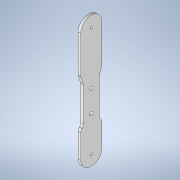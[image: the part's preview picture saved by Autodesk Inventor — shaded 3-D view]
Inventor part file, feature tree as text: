
AUTODESK INVENTOR PART (.ipt)
format: ipt  version: 2022 (Build 260153000, 153)  size: 157,184 bytes
history: native  units: mm
features: extrude x1, sketch x1
ambient origin geometry x8: Origin, YZ Plane, XZ Plane, XY Plane, X Axis, Y Axis, Z Axis, Center Point
bodies: Solid1 (feature_tree)
feature tree (2):
  extrude  "Extrusion1"  Depth=5.0mm
  sketch  "Sketch1"  dims[d16=3.0mm d17=0.0mm d44=4.0mm d46=8.0mm d47=9.0mm d48=9.0mm d50=8.0mm d53=24.0mm d54=3.0mm d57=4.0mm d59=8.0mm d60=9.0mm d61=9.0mm d63=8.0mm d64=40.0mm d65=25.0mm d100=5.0mm d102=3.0mm d103=0.5mm d104=0.872665mm d105=0.5mm d106=0.872665mm]
